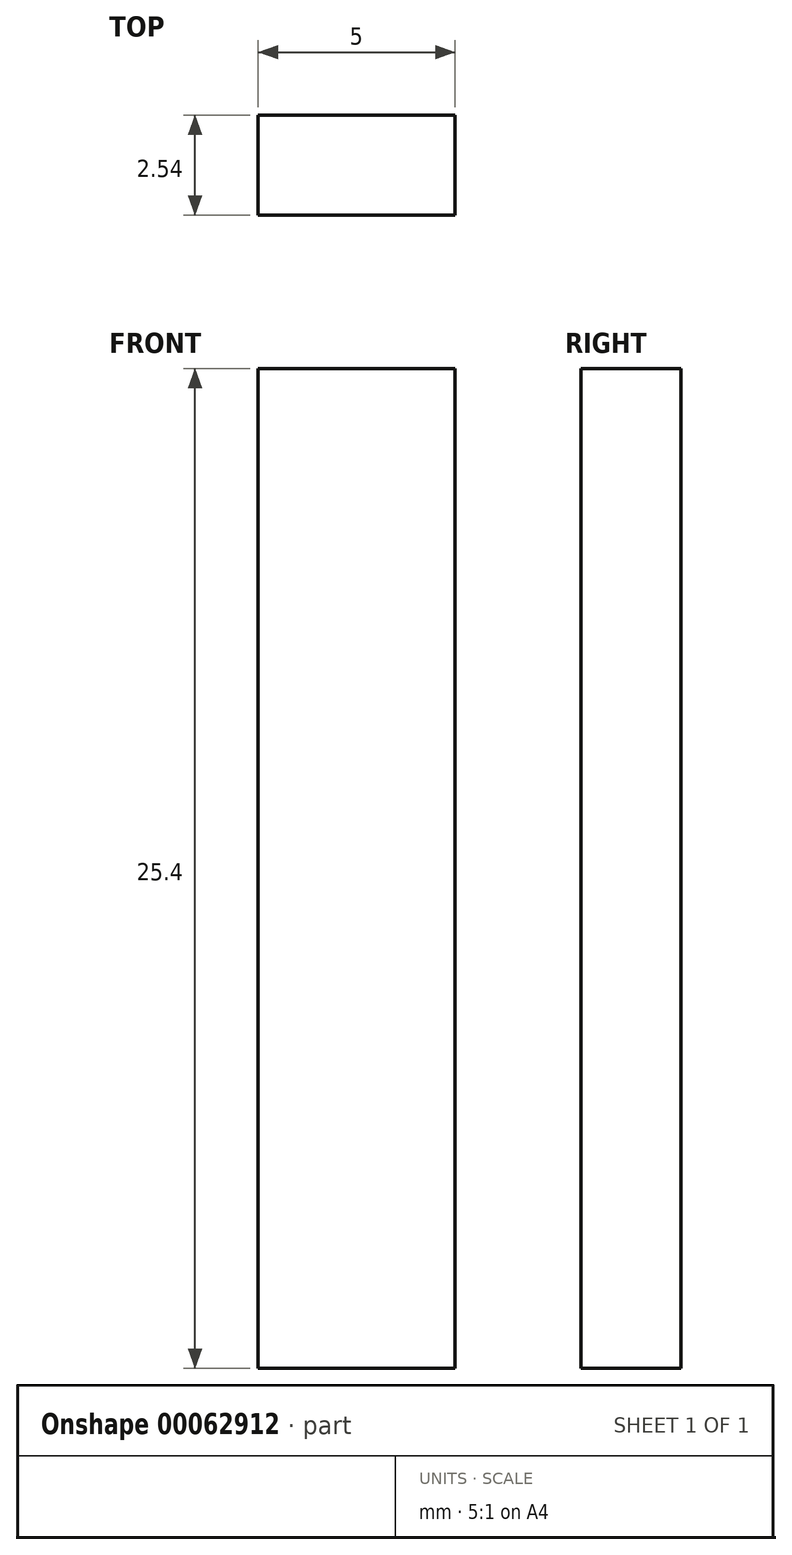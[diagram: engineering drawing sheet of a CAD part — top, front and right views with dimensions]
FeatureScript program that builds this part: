
annotation { "Feature Type Name" : "Feature", "Feature Type Description" : "" }
export const myFeature = defineFeature(function(context is Context, id is Id, definition is map)
    precondition{}
    {
        {
            var Q0;
            Q0=qCreatedBy(makeId("Front.planeOp"),FACE);
            var sketch = newSketch(context, id + "F0", { "sketchPlane" : qUnion([Q0])});
            skLineSegment(sketch, "E0.bottom", {"start": v(-2.5, -12.7) * mm, "end": v(2.5, -12.7) * mm});
            skLineSegment(sketch, "E0.top", {"start": v(-2.5, 12.7) * mm, "end": v(2.5, 12.7) * mm});
            skLineSegment(sketch, "E0.left", {"start": v(-2.5, -12.7) * mm, "end": v(-2.5, 12.7) * mm});
            skLineSegment(sketch, "E0.right", {"start": v(2.5, -12.7) * mm, "end": v(2.5, 12.7) * mm});
            skLineSegment(sketch, "E1", {"start": v(-2.5, -12.7) * mm, "end": v(2.5, 12.7) * mm, "construction": true});
            skSolve(sketch);
        }
        {
            var Q0;
            Q0=makeQuery(id+"F0.imprint","IMPRINT",FACE,{"disambiguationData":[TD([[makeQuery(id+"F0.imprint","IMPRINT",EDGE,{"derivedFrom":sQuery(id+"F0.wireOp",EDGE,"E0.bottom")}),1.0]])]});
            extrude(context, id + "F1", {"entities" : qUnion([Q0]), "depth" : 2.54 * mm});
        }
    });
